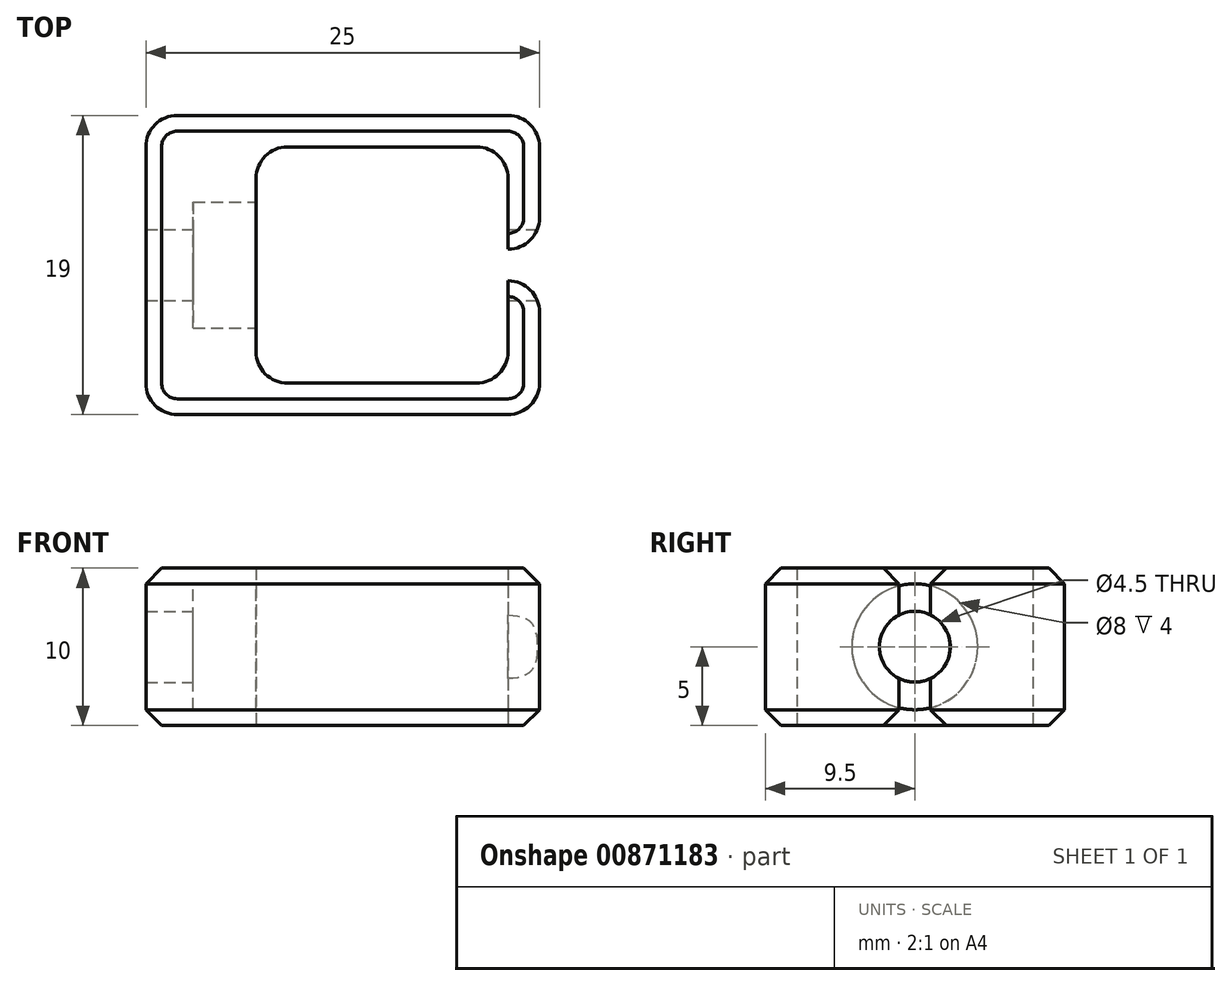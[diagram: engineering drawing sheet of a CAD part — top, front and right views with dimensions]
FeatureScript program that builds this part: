
annotation { "Feature Type Name" : "Feature", "Feature Type Description" : "" }
export const myFeature = defineFeature(function(context is Context, id is Id, definition is map)
    precondition{}
    {
        {
            var Q0;
            Q0=qCreatedBy(makeId("Top.planeOp"),FACE);
            var sketch = newSketch(context, id + "F0", { "sketchPlane" : qUnion([Q0])});
            skLineSegment(sketch, "E0.bottom", {"start": v(12.5, 9.5) * mm, "end": v(-12.5, 9.5) * mm});
            skLineSegment(sketch, "E0.top", {"start": v(12.5, -9.5) * mm, "end": v(-12.5, -9.5) * mm});
            skLineSegment(sketch, "E0.left", {"start": v(12.5, 9.5) * mm, "end": v(12.5, 1) * mm});
            skLineSegment(sketch, "E0.right", {"start": v(-12.5, 9.5) * mm, "end": v(-12.5, -9.5) * mm});
            skPoint(sketch, "E0.middle", {"position": v(0, 0) * mm});
            skLineSegment(sketch, "E1.bottom", {"start": v(-5.5, 7.5) * mm, "end": v(10.5, 7.5) * mm});
            skLineSegment(sketch, "E1.top", {"start": v(-5.5, -7.5) * mm, "end": v(10.5, -7.5) * mm});
            skLineSegment(sketch, "E1.left", {"start": v(-5.5, 7.5) * mm, "end": v(-5.5, -7.5) * mm});
            skLineSegment(sketch, "E1.right", {"start": v(10.5, 7.5) * mm, "end": v(10.5, 1) * mm});
            skLineSegment(sketch, "E2.bottom", {"start": v(12.5, -1) * mm, "end": v(10.5, -1) * mm});
            skLineSegment(sketch, "E2.top", {"start": v(12.5, 1) * mm, "end": v(10.5, 1) * mm});
            skPoint(sketch, "E2.middle", {"position": v(12.5, 0) * mm});
            skPoint(sketch, "E3.orphan", {"position": v(10, 1) * mm});
            skPoint(sketch, "E4.orphan", {"position": v(10, -1) * mm});
            skLineSegment(sketch, "E5.trimOffspring", {"start": v(10.5, -1) * mm, "end": v(10.5, -7.5) * mm});
            skLineSegment(sketch, "E6.trimOffspring", {"start": v(12.5, -1) * mm, "end": v(12.5, -9.5) * mm});
            skPoint(sketch, "E2.left.end.orphan", {"position": v(15, 1) * mm});
            skPoint(sketch, "E7.orphan", {"position": v(15, -1) * mm});
            skSolve(sketch);
        }
        {
            var Q0;
            Q0=makeQuery(id+"F0.imprint","IMPRINT",FACE,{"disambiguationData":[TD([[makeQuery(id+"F0.imprint","IMPRINT",EDGE,{"derivedFrom":sQuery(id+"F0.wireOp",EDGE,"E0.bottom")}),1.0]])]});
            extrude(context, id + "F1", {"entities" : qUnion([Q0]), "endBound" : BoundingType.SYMMETRIC, "depth" : 10 * mm, "offsetDistance" : 25 * mm});
        }
        {
            var Q0;
            Q0=makeQuery(id+"F1.opExtrude","SWEPT_FACE",FACE,{"disambiguationData":[OSD([sQuery(id+"F0.wireOp",EDGE,"E1.left")])]});
            var sketch = newSketch(context, id + "F2", { "sketchPlane" : qUnion([Q0])});
            skCircle(sketch, "E8", {"center": v(0, 0) * mm, "radius": 2.25 * mm});
            skSolve(sketch);
        }
        {
            var Q0;
            Q0 = qSketchRegion(id + "F2", true);
            extrude(context, id + "F3", {"entities" : qUnion([Q0]), "operationType" : NewBodyOperationType.REMOVE, "endBound" : BoundingType.SYMMETRIC, "oppositeDirection" : true, "depth" : 200 * mm, "offsetDistance" : 25 * mm});
        }
        {
            var Q0;
            Q0=makeQuery(id+"F1.opExtrude","SWEPT_FACE",FACE,{"disambiguationData":[OSD([sQuery(id+"F0.wireOp",EDGE,"E1.left")])]});
            var sketch = newSketch(context, id + "F4", { "sketchPlane" : qUnion([Q0])});
            skCircle(sketch, "E9", {"center": v(0, 0) * mm, "radius": 4 * mm});
            skSolve(sketch);
        }
        {
            var Q0;
            Q0 = qSketchRegion(id + "F4", true);
            extrude(context, id + "F5", {"entities" : qUnion([Q0]), "operationType" : NewBodyOperationType.REMOVE, "oppositeDirection" : true, "depth" : 4 * mm, "offsetDistance" : 25 * mm});
        }
        {
            var Q0;
            Q0=makeQuery(id+"F1.opExtrude","SWEPT_EDGE",EDGE,{"disambiguationData":[OSD([sQuery(id+"F0.wireOp",EDGE,"E0.bottom"),sQuery(id+"F0.wireOp",EDGE,"E0.right")])]});
            var Q1;
            Q1=makeQuery(id+"F1.opExtrude","SWEPT_EDGE",EDGE,{"disambiguationData":[OSD([sQuery(id+"F0.wireOp",EDGE,"E0.top"),sQuery(id+"F0.wireOp",EDGE,"E0.right")])]});
            var Q2;
            Q2=makeQuery(id+"F1.opExtrude","SWEPT_EDGE",EDGE,{"disambiguationData":[OSD([sQuery(id+"F0.wireOp",EDGE,"E0.bottom"),sQuery(id+"F0.wireOp",EDGE,"E0.left")])]});
            var Q3;
            Q3=makeQuery(id+"F1.opExtrude","SWEPT_EDGE",EDGE,{"disambiguationData":[OSD([sQuery(id+"F0.wireOp",EDGE,"E0.top"),sQuery(id+"F0.wireOp",EDGE,"E6.trimOffspring")])]});
            var Q4;
            Q4=makeQuery(id+"F1.opExtrude","SWEPT_EDGE",EDGE,{"disambiguationData":[OSD([sQuery(id+"F0.wireOp",EDGE,"E1.top"),sQuery(id+"F0.wireOp",EDGE,"E5.trimOffspring")])]});
            var Q5;
            Q5=makeQuery(id+"F1.opExtrude","SWEPT_EDGE",EDGE,{"disambiguationData":[OSD([sQuery(id+"F0.wireOp",EDGE,"E1.bottom"),sQuery(id+"F0.wireOp",EDGE,"E1.right")])]});
            var Q6;
            Q6=makeQuery(id+"F1.opExtrude","SWEPT_EDGE",EDGE,{"disambiguationData":[OSD([sQuery(id+"F0.wireOp",EDGE,"E2.bottom"),sQuery(id+"F0.wireOp",EDGE,"E6.trimOffspring")])]});
            var Q7;
            Q7=makeQuery(id+"F1.opExtrude","SWEPT_EDGE",EDGE,{"disambiguationData":[OSD([sQuery(id+"F0.wireOp",EDGE,"E0.left"),sQuery(id+"F0.wireOp",EDGE,"E2.top")])]});
            var Q8;
            Q8=makeQuery(id+"F1.opExtrude","SWEPT_EDGE",EDGE,{"disambiguationData":[OSD([sQuery(id+"F0.wireOp",EDGE,"E1.bottom"),sQuery(id+"F0.wireOp",EDGE,"E1.left")])]});
            var Q9;
            Q9=makeQuery(id+"F1.opExtrude","SWEPT_EDGE",EDGE,{"disambiguationData":[OSD([sQuery(id+"F0.wireOp",EDGE,"E1.top"),sQuery(id+"F0.wireOp",EDGE,"E1.left")])]});
            fillet(context, id + "F6", {"entities" : qUnion([Q0, Q1, Q2, Q3, Q4, Q5, Q6, Q7, Q8, Q9]), "tangentPropagation" : true, "radius" : 2 * mm, "defaultsChanged" : false, "vertexSettings" : [], "allowEdgeOverflow" : false});
        }
        {
            var Q0;
            Q0=makeQuery(id+"F1.opExtrude","CAP_EDGE",EDGE,{"disambiguationData":[OSD([sQuery(id+"F0.wireOp",EDGE,"E0.bottom")])],"isStart":false});
            var Q1;
            Q1=makeQuery(id+"F1.opExtrude","CAP_EDGE",EDGE,{"disambiguationData":[OSD([sQuery(id+"F0.wireOp",EDGE,"E0.right")])],"isStart":true});
            chamfer(context, id + "F7", {"entities" : qUnion([Q0, Q1]), "width" : 1 * mm, "tangentPropagation" : true});
        }
    });
